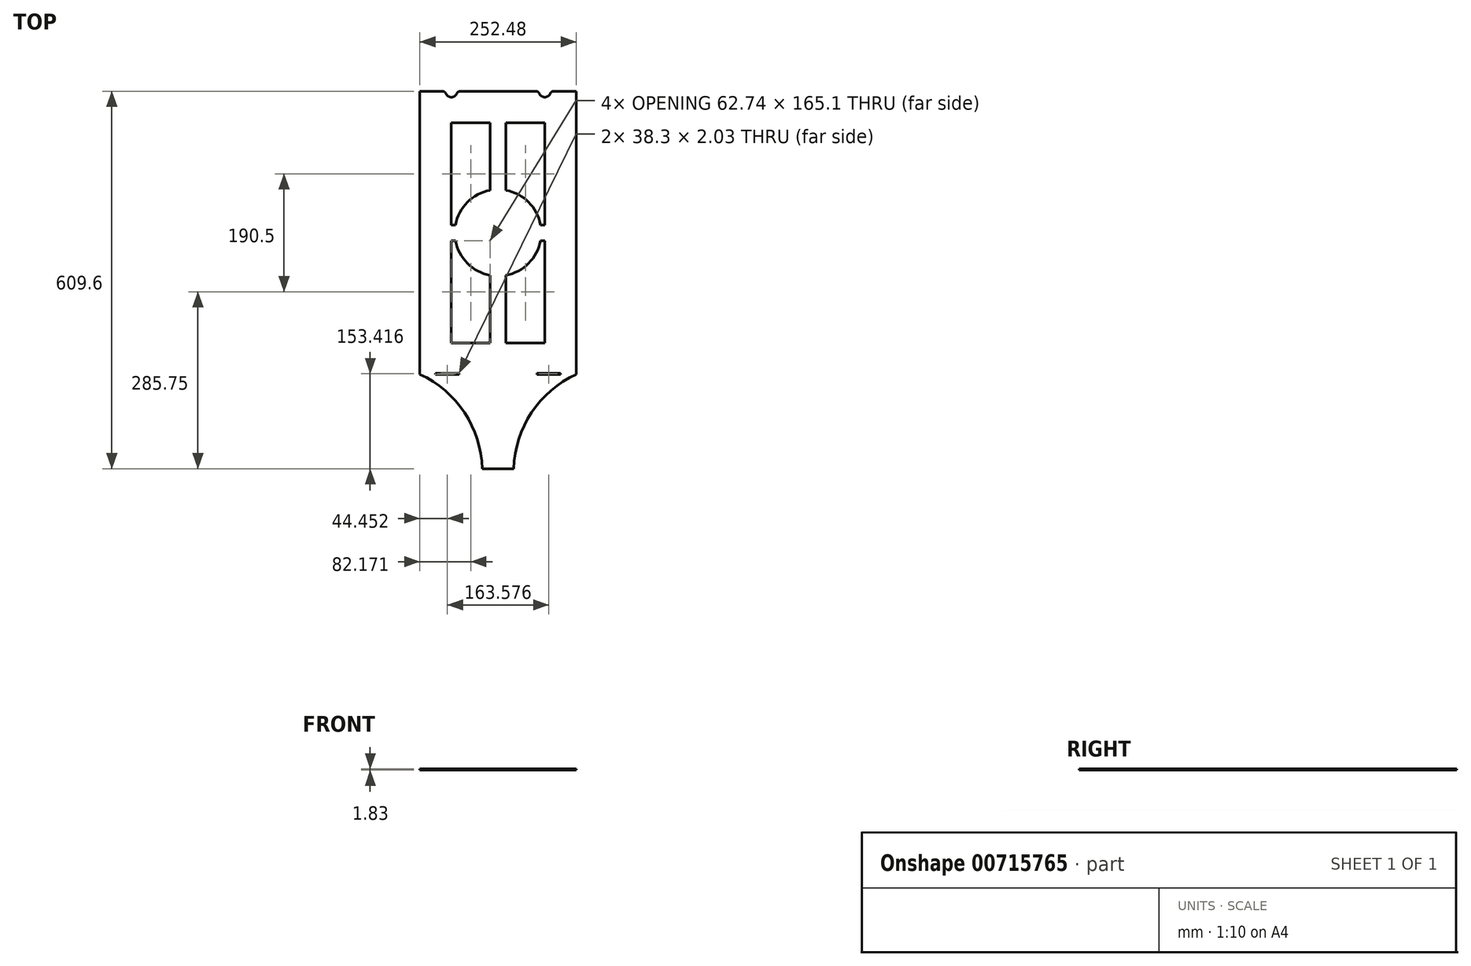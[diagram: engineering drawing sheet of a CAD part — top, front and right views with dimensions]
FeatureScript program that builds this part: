
annotation { "Feature Type Name" : "Feature", "Feature Type Description" : "" }
export const myFeature = defineFeature(function(context is Context, id is Id, definition is map)
    precondition{}
    {
        {
            var Q0;
            Q0=qCreatedBy(makeId("Top.planeOp"),FACE);
            var sketch = newSketch(context, id + "F0", { "sketchPlane" : qUnion([Q0])});
            skLineSegment(sketch, "E0.bottom", {"start": v(-126.24, 304.8) * mm, "end": v(-89.99, 304.8) * mm});
            skLineSegment(sketch, "E0.top", {"start": v(-25.4, -304.8) * mm, "end": v(25.4, -304.8) * mm});
            skLineSegment(sketch, "E0.left", {"start": v(-126.24, 304.8) * mm, "end": v(-126.24, -152.4) * mm});
            skLineSegment(sketch, "E0.right", {"start": v(126.24, 304.8) * mm, "end": v(126.24, -152.4) * mm});
            skLineSegment(sketch, "E1", {"start": v(-126.24, -304.8) * mm, "end": v(126.24, 304.8) * mm, "construction": true});
            skLineSegment(sketch, "E2", {"start": v(-126.24, 304.8) * mm, "end": v(126.24, -304.8) * mm, "construction": true});
            skLineSegment(sketch, "E3", {"start": v(-126.24, -152.4) * mm, "end": v(126.24, -152.4) * mm});
            skPoint(sketch, "E4.endSnap0", {"position": v(0, -304.8) * mm});
            skArc(sketch, "E5", {"start": v(-25.4, -304.8) * mm, "mid": v(-54.05, -214.2) * mm, "end": v(-126.24, -152.4) * mm});
            skPoint(sketch, "E5.startSnap0", {"position": v(-25.4, -305.1) * mm});
            skArc(sketch, "E6.MirrorCS", {"start": v(25.4, -304.8) * mm, "mid": v(54.05, -214.2) * mm, "end": v(126.24, -152.4) * mm});
            skLineSegment(sketch, "E7.bottom", {"start": v(-100.94, -152.4) * mm, "end": v(-62.64, -152.4) * mm});
            skLineSegment(sketch, "E7.top", {"start": v(-100.94, -150.37) * mm, "end": v(-62.64, -150.37) * mm});
            skLineSegment(sketch, "E7.left", {"start": v(-100.94, -152.4) * mm, "end": v(-100.94, -150.37) * mm});
            skLineSegment(sketch, "E7.right", {"start": v(-62.64, -152.4) * mm, "end": v(-62.64, -150.37) * mm});
            skLineSegment(sketch, "E8.bottom", {"start": v(62.64, -152.4) * mm, "end": v(100.94, -152.4) * mm});
            skLineSegment(sketch, "E8.top", {"start": v(62.64, -150.37) * mm, "end": v(100.94, -150.37) * mm});
            skLineSegment(sketch, "E8.left", {"start": v(62.64, -152.4) * mm, "end": v(62.64, -150.37) * mm});
            skLineSegment(sketch, "E8.right", {"start": v(100.94, -152.4) * mm, "end": v(100.94, -150.37) * mm});
            skArc(sketch, "E9", {"start": v(-84.17, 300.99) * mm, "mid": v(-75.44, 295.28) * mm, "end": v(-66.7, 300.99) * mm});
            skArc(sketch, "E10", {"start": v(66.7, 301) * mm, "mid": v(75.44, 295.28) * mm, "end": v(84.17, 301) * mm});
            skLineSegment(sketch, "E11.trimOffspring", {"start": v(89.99, 304.8) * mm, "end": v(126.24, 304.8) * mm});
            skLineSegment(sketch, "E12.trimOffspring", {"start": v(-60.89, 304.8) * mm, "end": v(60.89, 304.8) * mm});
            skPoint(sketch, "E13.visualSharp", {"position": v(-84.96, 304.8) * mm});
            skArc(sketch, "E13.filletArc", {"start": v(-84.17, 300.99) * mm, "mid": v(-86.5, 303.76) * mm, "end": v(-89.99, 304.8) * mm});
            skPoint(sketch, "E14.visualSharp", {"position": v(-65.91, 304.8) * mm});
            skArc(sketch, "E14.filletArc", {"start": v(-60.89, 304.8) * mm, "mid": v(-64.37, 303.76) * mm, "end": v(-66.7, 300.99) * mm});
            skPoint(sketch, "E15.visualSharp", {"position": v(65.91, 304.8) * mm});
            skArc(sketch, "E15.filletArc", {"start": v(66.7, 301) * mm, "mid": v(64.37, 303.76) * mm, "end": v(60.89, 304.8) * mm});
            skPoint(sketch, "E16.visualSharp", {"position": v(84.96, 304.8) * mm});
            skArc(sketch, "E16.filletArc", {"start": v(89.99, 304.8) * mm, "mid": v(86.5, 303.76) * mm, "end": v(84.17, 301) * mm});
            skLineSegment(sketch, "E17.bottom", {"start": v(-75.44, 254) * mm, "end": v(-12.7, 254) * mm});
            skLineSegment(sketch, "E17.top", {"start": v(-75.44, -101.6) * mm, "end": v(-12.7, -101.6) * mm});
            skLineSegment(sketch, "E17.left", {"start": v(-75.44, 254) * mm, "end": v(-75.44, 88.9) * mm});
            skLineSegment(sketch, "E17.right", {"start": v(75.44, 254) * mm, "end": v(75.44, 88.9) * mm});
            skLineSegment(sketch, "E18", {"start": v(75.44, 254) * mm, "end": v(-75.44, -101.6) * mm, "construction": true});
            skLineSegment(sketch, "E19", {"start": v(-75.44, 254) * mm, "end": v(75.44, -101.6) * mm, "construction": true});
            skArc(sketch, "E20", {"start": v(12.7, 7.51) * mm, "mid": v(49.4, 26.8) * mm, "end": v(68.69, 63.5) * mm});
            skLineSegment(sketch, "E21", {"start": v(12.7, -101.6) * mm, "end": v(12.7, 7.51) * mm});
            skLineSegment(sketch, "E22", {"start": v(-12.7, -101.6) * mm, "end": v(-12.7, 7.51) * mm});
            skPoint(sketch, "E23.orphan", {"position": v(-12.7, -311) * mm});
            skPoint(sketch, "E24.orphan", {"position": v(12.7, -313.54) * mm});
            skPoint(sketch, "E25.end.orphan", {"position": v(25.4, -313.54) * mm});
            skPoint(sketch, "E26.orphan", {"position": v(-25.4, -313.26) * mm});
            skPoint(sketch, "E27.orphan", {"position": v(-25.4, -296.94) * mm});
            skPoint(sketch, "E28.orphan", {"position": v(0, -311) * mm});
            skPoint(sketch, "E4.end.orphan", {"position": v(0, -297.5) * mm});
            skLineSegment(sketch, "E29.trimOffspring", {"start": v(12.7, -101.6) * mm, "end": v(75.44, -101.6) * mm});
            skArc(sketch, "E30.trimOffspring", {"start": v(-12.7, 144.89) * mm, "mid": v(-49.4, 125.6) * mm, "end": v(-68.69, 88.9) * mm});
            skLineSegment(sketch, "E31.trimOffspring", {"start": v(12.7, 144.89) * mm, "end": v(12.7, 254) * mm});
            skLineSegment(sketch, "E32.trimOffspring", {"start": v(-12.7, 144.89) * mm, "end": v(-12.7, 254) * mm});
            skLineSegment(sketch, "E33", {"start": v(-75.44, 88.9) * mm, "end": v(-68.69, 88.9) * mm});
            skLineSegment(sketch, "E34", {"start": v(-75.44, 63.5) * mm, "end": v(-68.69, 63.5) * mm});
            skLineSegment(sketch, "E35.trimOffspring", {"start": v(68.69, 88.9) * mm, "end": v(75.44, 88.9) * mm});
            skArc(sketch, "E36.trimOffspring", {"start": v(68.69, 88.9) * mm, "mid": v(49.4, 125.6) * mm, "end": v(12.7, 144.89) * mm});
            skArc(sketch, "E37.trimOffspring", {"start": v(-68.69, 63.5) * mm, "mid": v(-49.4, 26.8) * mm, "end": v(-12.7, 7.51) * mm});
            skLineSegment(sketch, "E38.trimOffspring", {"start": v(68.69, 63.5) * mm, "end": v(75.44, 63.5) * mm});
            skLineSegment(sketch, "E39.trimOffspring", {"start": v(75.44, 63.5) * mm, "end": v(75.44, -101.6) * mm});
            skLineSegment(sketch, "E40.trimOffspring", {"start": v(-75.44, 63.5) * mm, "end": v(-75.44, -101.6) * mm});
            skLineSegment(sketch, "E41.trimOffspring", {"start": v(12.7, 254) * mm, "end": v(75.44, 254) * mm});
            skSolve(sketch);
        }
        {
            var Q0;
            Q0 = qSketchRegion(id + "F0", true);
            extrude(context, id + "F1", {"entities" : qUnion([Q0]), "depth" : 1.83 * mm, "offsetDistance" : 25.4 * mm});
        }
    });
